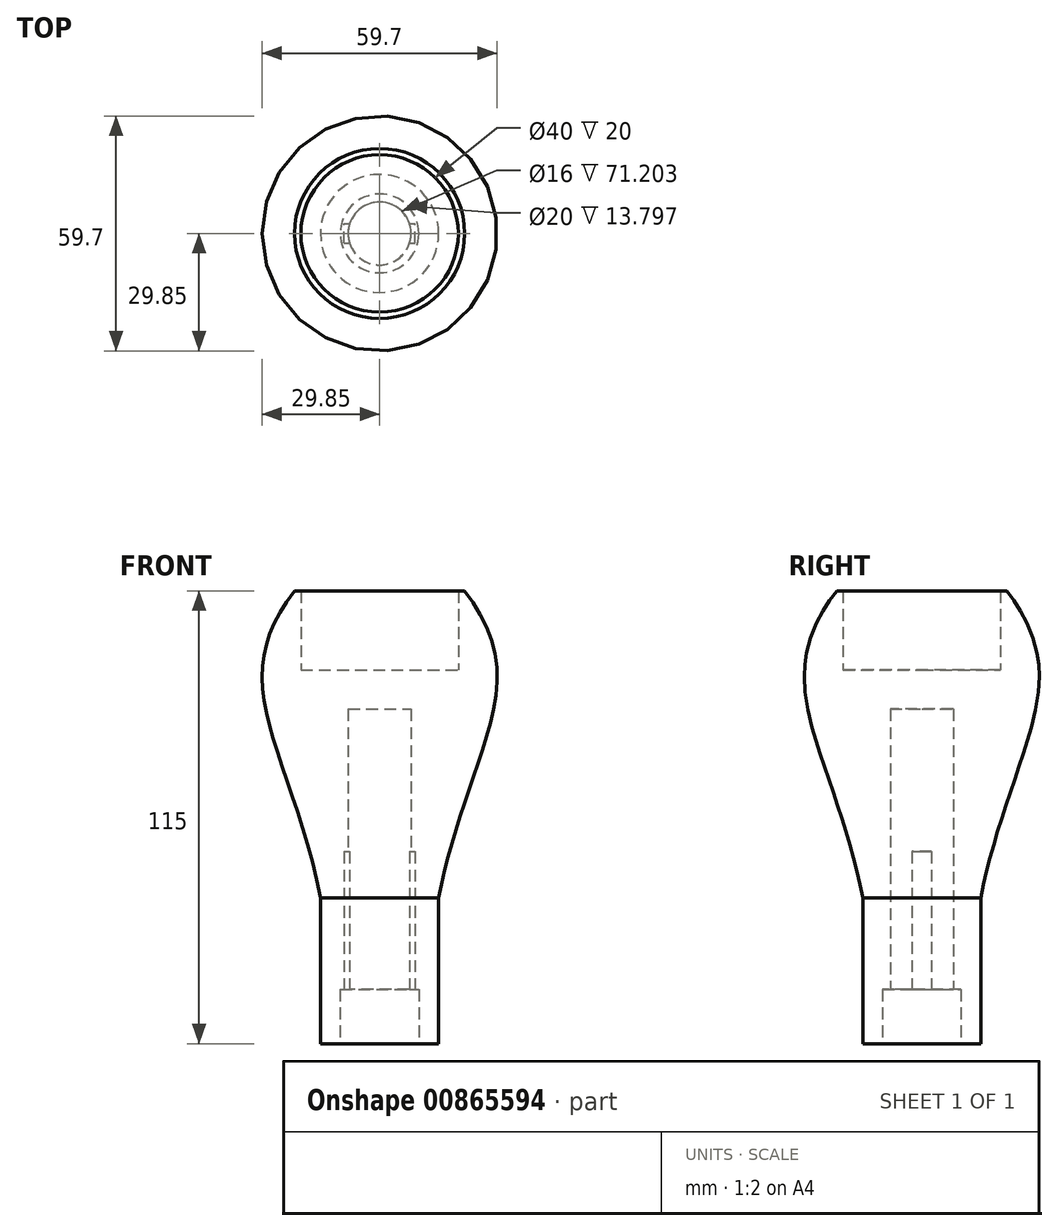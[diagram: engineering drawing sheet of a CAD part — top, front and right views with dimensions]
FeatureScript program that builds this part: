
annotation { "Feature Type Name" : "Feature", "Feature Type Description" : "" }
export const myFeature = defineFeature(function(context is Context, id is Id, definition is map)
    precondition{}
    {
        {
            var Q0;
            Q0=qCreatedBy(makeId("Front.planeOp"),FACE);
            var sketch = newSketch(context, id + "F0", { "sketchPlane" : qUnion([Q0])});
            skLineSegment(sketch, "E0", {"start": v(15, 0) * mm, "end": v(15, 37) * mm});
            skFitSpline(sketch, "E1", {"points": [v(15, 37) * mm, v(29.5, 88.19) * mm, v(21.6, 115) * mm], "startDerivative": vector(20.88, 109.79) * mm, "endDerivative": vector(-49.64, 64.35) * mm});
            skLineSegment(sketch, "E2", {"start": v(21.6, 115) * mm, "end": v(21.6, 115) * mm});
            skLineSegment(sketch, "E3", {"start": v(21.6, 115) * mm, "end": v(20, 115) * mm});
            skLineSegment(sketch, "E4", {"start": v(20, 115) * mm, "end": v(20, 95) * mm});
            skLineSegment(sketch, "E5", {"start": v(20, 95) * mm, "end": v(0, 95) * mm});
            skLineSegment(sketch, "E6", {"start": v(10, 0) * mm, "end": v(10, 13.8) * mm});
            skLineSegment(sketch, "E7", {"start": v(15, 0) * mm, "end": v(10, 0) * mm});
            skLineSegment(sketch, "E8", {"start": v(10, 13.8) * mm, "end": v(8, 13.8) * mm});
            skLineSegment(sketch, "E9", {"start": v(8, 13.8) * mm, "end": v(8, 85) * mm});
            skLineSegment(sketch, "E10", {"start": v(8, 85) * mm, "end": v(0, 85) * mm});
            skLineSegment(sketch, "E11", {"start": v(0, 85) * mm, "end": v(0, 95) * mm});
            skSolve(sketch);
        }
        {
            var Q0;
            Q0=makeQuery(id+"F0.imprint","IMPRINT",FACE,{"disambiguationData":[TD([[makeQuery(id+"F0.imprint","IMPRINT",EDGE,{"derivedFrom":sQuery(id+"F0.wireOp",EDGE,"E0")}),1.0]])]});
            var Q1;
            Q1=sQuery(id+"F0.wireOp",EDGE,"E11");
            revolve(context, id + "F1", {"surfaceOperationType" : NewSurfaceOperationType.NEW, "entities" : qUnion([Q0]), "axis" : qUnion([Q1]), "revolveType" : RevolveType.FULL});
        }
        {
            var Q0;
            Q0=makeQuery(id+"F1.opRevolve","SWEPT_FACE",FACE,{"disambiguationData":[OSD([sQuery(id+"F0.wireOp",EDGE,"E8")])]});
            var sketch = newSketch(context, id + "F2", { "sketchPlane" : qUnion([Q0])});
            skLineSegment(sketch, "E12.bottom", {"start": v(-9, 2.5) * mm, "end": v(9, 2.5) * mm});
            skLineSegment(sketch, "E12.top", {"start": v(-9, -2.5) * mm, "end": v(9, -2.5) * mm});
            skLineSegment(sketch, "E12.left", {"start": v(-9, 2.5) * mm, "end": v(-9, -2.5) * mm});
            skLineSegment(sketch, "E12.right", {"start": v(9, 2.5) * mm, "end": v(9, -2.5) * mm});
            skSolve(sketch);
        }
        {
            var Q0;
            {var subQ0=sQuery(id+"F2.wireOp",EDGE,"E12.left");Q0=makeQuery(id+"F2.imprint","IMPRINT",FACE,{"disambiguationData":[TD([[makeQuery(id+"F2.imprint","IMPRINT",EDGE,{"derivedFrom":subQ0}),1.0]])]});}
            var Q1;
            {var subQ0=sQuery(id+"F2.wireOp",EDGE,"E12.right");Q1=makeQuery(id+"F2.imprint","IMPRINT",FACE,{"disambiguationData":[TD([[makeQuery(id+"F2.imprint","IMPRINT",EDGE,{"derivedFrom":subQ0}),-1.0]])]});}
            extrude(context, id + "F3", {"entities" : qUnion([Q0, Q1]), "operationType" : NewBodyOperationType.REMOVE, "oppositeDirection" : true, "depth" : 35 * mm, "offsetDistance" : 25 * mm});
        }
    });
